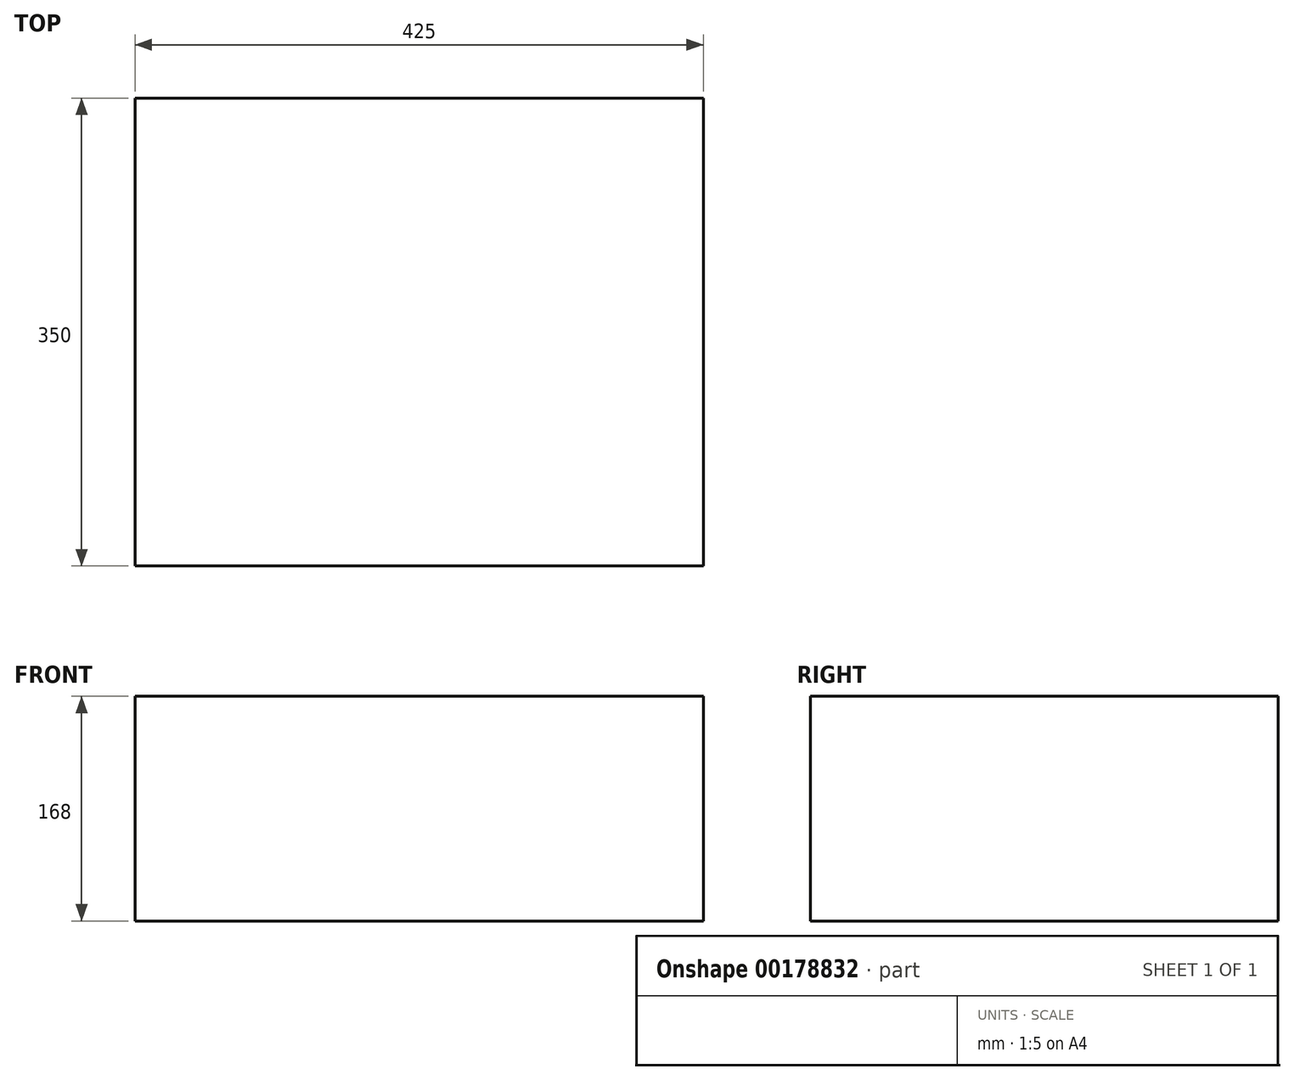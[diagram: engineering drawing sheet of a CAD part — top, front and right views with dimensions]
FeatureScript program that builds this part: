
annotation { "Feature Type Name" : "Feature", "Feature Type Description" : "" }
export const myFeature = defineFeature(function(context is Context, id is Id, definition is map)
    precondition{}
    {
        {
            var Q0;
            Q0=qCreatedBy(makeId("Front.planeOp"),FACE);
            var sketch = newSketch(context, id + "F0", { "sketchPlane" : qUnion([Q0])});
            skLineSegment(sketch, "E0.bottom", {"start": v(-215.5, 76.6) * mm, "end": v(209.5, 76.6) * mm});
            skLineSegment(sketch, "E0.top", {"start": v(-215.5, -91.4) * mm, "end": v(209.5, -91.4) * mm});
            skLineSegment(sketch, "E0.left", {"start": v(-215.5, 76.6) * mm, "end": v(-215.5, -91.4) * mm});
            skLineSegment(sketch, "E0.right", {"start": v(209.5, 76.6) * mm, "end": v(209.5, -91.4) * mm});
            skSolve(sketch);
        }
        {
            var Q0;
            Q0=makeQuery(id+"F0.imprint","IMPRINT",FACE,{"disambiguationData":[TD([[makeQuery(id+"F0.imprint","IMPRINT",EDGE,{"derivedFrom":sQuery(id+"F0.wireOp",EDGE,"E0.bottom")}),-1.0]])]});
            extrude(context, id + "F1", {"entities" : qUnion([Q0]), "depth" : 350 * mm});
        }
    });
